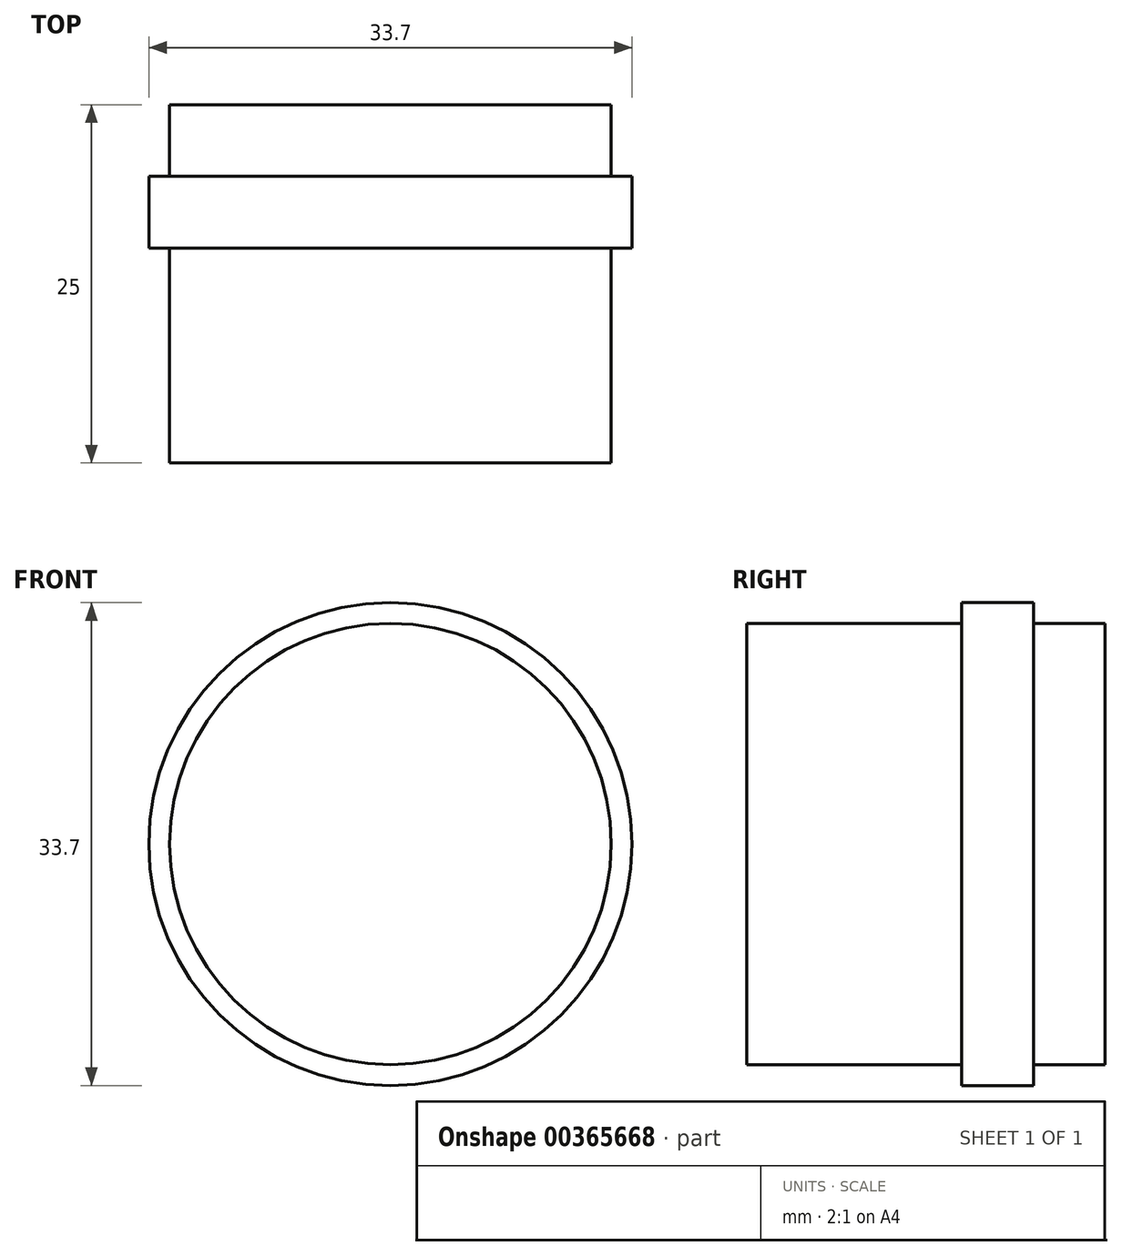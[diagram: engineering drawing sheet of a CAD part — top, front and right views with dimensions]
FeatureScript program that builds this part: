
annotation { "Feature Type Name" : "Feature", "Feature Type Description" : "" }
export const myFeature = defineFeature(function(context is Context, id is Id, definition is map)
    precondition{}
    {
        {
            var Q0;
            Q0=qCreatedBy(makeId("Front.planeOp"),FACE);
            var sketch = newSketch(context, id + "F0", { "sketchPlane" : qUnion([Q0])});
            skCircle(sketch, "E0", {"center": v(0, 0) * mm, "radius": 16.85 * mm});
            skSolve(sketch);
        }
        {
            var Q0;
            Q0 = qSketchRegion(id + "F0", true);
            extrude(context, id + "F1", {"entities" : qUnion([Q0]), "oppositeDirection" : true, "depth" : 25 * mm});
        }
        {
            var Q0;
            Q0=qCreatedBy(makeId("Front.planeOp"),FACE);
            var sketch = newSketch(context, id + "F2", { "sketchPlane" : qUnion([Q0])});
            skCircle(sketch, "E1", {"center": v(0, 0) * mm, "radius": 22.41 * mm});
            skCircle(sketch, "E2", {"center": v(0, 0) * mm, "radius": 15.4 * mm});
            skSolve(sketch);
        }
        {
            var Q0;
            Q0 = qSketchRegion(id + "F2", true);
            extrude(context, id + "F3", {"entities" : qUnion([Q0]), "operationType" : NewBodyOperationType.REMOVE, "oppositeDirection" : true, "depth" : 15 * mm});
        }
        {
            var Q0;
            Q0=makeQuery(id+"F1.opExtrude","CAP_FACE",FACE,{"disambiguationData":[OSD([sQuery(id+"F0.wireOp",EDGE,"E0")])],"isStart":false});
            var sketch = newSketch(context, id + "F4", { "sketchPlane" : qUnion([Q0])});
            skCircle(sketch, "E3", {"center": v(0, 0) * mm, "radius": 22.66 * mm});
            skCircle(sketch, "E4", {"center": v(0, 0) * mm, "radius": 15.4 * mm});
            skSolve(sketch);
        }
        {
            var Q0;
            Q0 = qSketchRegion(id + "F4", true);
            extrude(context, id + "F5", {"entities" : qUnion([Q0]), "operationType" : NewBodyOperationType.REMOVE, "oppositeDirection" : true, "depth" : 5 * mm});
        }
    });
